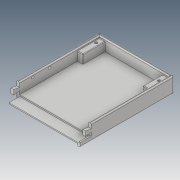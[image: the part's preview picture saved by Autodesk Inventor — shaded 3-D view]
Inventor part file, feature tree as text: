
AUTODESK INVENTOR PART (.ipt)
format: ipt  version: 2019 (Build 230136000, 136)  size: 354,816 bytes
history: native  units: mm
features: extrude x7, sketch x7, other x7, fillet x2, direct_edit x2, projected_geometry x2, surface_op x1, plane x1
ambient origin geometry x8: Origin, YZ Plane, XZ Plane, XY Plane, X Axis, Y Axis, Z Axis, Center Point
bodies: Solid1 (feature_tree)
feature tree (29):
  extrude  "Extrusion1"  Depth=170.0mm
  extrude  "Extrusion2"  Depth=5.0mm
  extrude  "Extrusion3"  Depth=25.0mm TaperAngle=0.0deg
  fillet  "Fillet1"  Radius=2.0mm
  surface_op  "Sculpt2"
  extrude  "Extrusion4"  TaperAngle=0.0deg  [1 undecoded]
  extrude  "Extrusion5"  Depth=40.0mm
  fillet  "Fillet2"  [1 undecoded]
  extrude  "Extrusion7"  Depth=35.0mm
  plane  "Work Plane1"
  extrude  "Extrusion8"  Depth=16.0mm TaperAngle=0.0deg
  direct_edit  "Direct Edit1"
  direct_edit  "Direct Edit2"
  sketch  "Sketch1"  dims[d0=135.0mm d1=170.0mm]
  sketch  "Sketch2"  dims[d2=28.0mm d3=0.0mm d4=5.0mm]
  projected_geometry  "Projected Loop1"
  sketch  "Sketch3"  dims[d5=20.0mm d6=0.0mm d7=25.0mm d8=0.0mm d9=2.0mm]
  projected_geometry  "Projected Loop2"
  sketch  "Sketch4"  dims[d10=0.0mm d11=0.0mm]
  sketch  "Sketch5"  dims[d12=10.0mm d13=40.0mm d14=0.0mm]
  sketch  "Sketch6"  dims[d15=0.0mm d16=35.0mm]
  sketch  "Sketch7"  dims[d17=11.0mm d18=16.0mm d19=0.0mm d20=4.5mm d22=4.0mm d23=4.5mm d24=6.5mm d26=12.0mm d27=0.0mm d28=1.0mm d29=4.5mm d30=4.5mm d31=30.8mm d32=5.0mm d34=90.0mm d37=0.0mm d38=0.0mm d39=-1.5mm d40=7.5mm d41=7.5mm d42=3.15mm d43=0.0mm d44=10.0mm d45=12.5mm d46=-0.5mm d47=-0.5mm]
  other  "Composite2"
  other  "Srf2"
  other  "Size1"
  other  "Size2"
  parser-record x1  (decoder bookkeeping rows leaked as tree rows — omitted from the tree; the rows remain in map.json)
  other  "CaseA.iam"
  other  "Case_A1:1"
note: 2 required parameter values undecoded (feature->parameter linkage not recoverable at this tier; creation-order binding heuristic only, values carry confidence <= 0.55)
note: 1 file-system path scrubbed to <path> (originals preserved in map.json)
